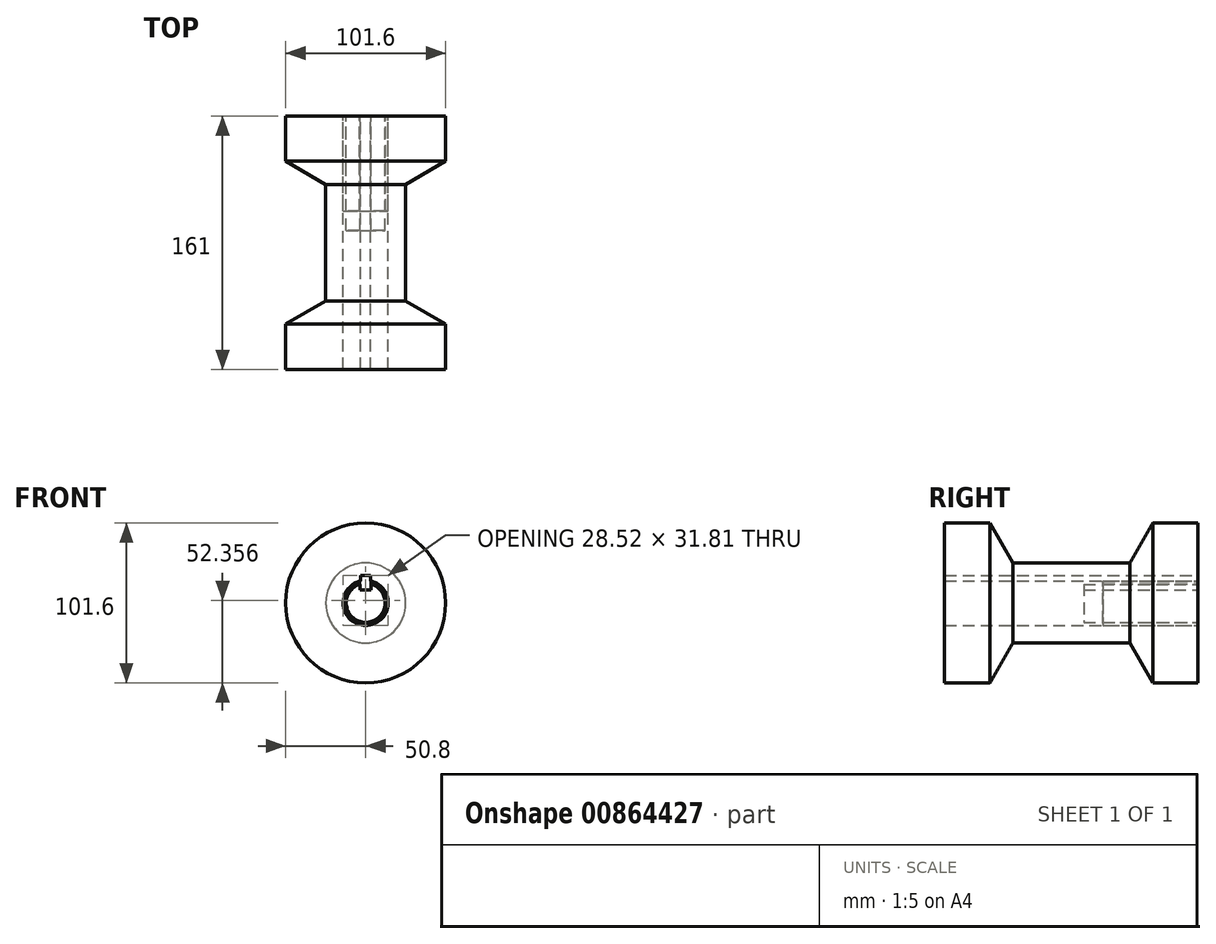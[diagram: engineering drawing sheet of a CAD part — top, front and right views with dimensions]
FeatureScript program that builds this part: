
annotation { "Feature Type Name" : "Feature", "Feature Type Description" : "" }
export const myFeature = defineFeature(function(context is Context, id is Id, definition is map)
    precondition{}
    {
        {
            var Q0;
            Q0=qCreatedBy(makeId("Front.planeOp"),FACE);
            var sketch = newSketch(context, id + "F0", { "sketchPlane" : qUnion([Q0])});
            skCircle(sketch, "E0", {"center": v(0, 0) * mm, "radius": 14.29 * mm});
            skCircle(sketch, "E1", {"center": v(0, 0) * mm, "radius": 12.5 * mm});
            skSolve(sketch);
        }
        {
            var Q0;
            Q0 = qSketchRegion(id + "F0", true);
            extrude(context, id + "F1", {"entities" : qUnion([Q0]), "depth" : 60.32 * mm, "offsetDistance" : 25.4 * mm});
        }
        {
            var Q0;
            Q0=qCreatedBy(makeId("Front.planeOp"),FACE);
            var sketch = newSketch(context, id + "F2", { "sketchPlane" : qUnion([Q0])});
            skLineSegment(sketch, "E2.bottom", {"start": v(-3.82, 0) * mm, "end": v(3.18, 0) * mm, "construction": true});
            skLineSegment(sketch, "E2.top", {"start": v(-3.83, 6.82) * mm, "end": v(3.18, 6.82) * mm});
            skLineSegment(sketch, "E2.left", {"start": v(-3.82, 0) * mm, "end": v(-3.83, 6.82) * mm, "construction": true});
            skLineSegment(sketch, "E2.right", {"start": v(3.18, 0) * mm, "end": v(3.18, 6.82) * mm, "construction": true});
            skPoint(sketch, "E3", {"position": v(0, -14.29) * mm});
            skLineSegment(sketch, "E4.0", {"start": v(-3.83, 13.65) * mm, "end": v(3.18, 13.65) * mm});
            skLineSegment(sketch, "E5", {"start": v(-3.83, 13.65) * mm, "end": v(-3.83, 6.82) * mm});
            skLineSegment(sketch, "E6", {"start": v(3.18, 13.65) * mm, "end": v(3.18, 6.82) * mm});
            skSolve(sketch);
        }
        {
            var Q0;
            Q0 = qSketchRegion(id + "F2", true);
            extrude(context, id + "F3", {"entities" : qUnion([Q0]), "operationType" : NewBodyOperationType.REMOVE, "endBound" : BoundingType.THROUGH_ALL, "depth" : 59.53 * mm, "offsetDistance" : 25.4 * mm});
        }
        {
            var Q0;
            Q0=qCreatedBy(makeId("Front.planeOp"),FACE);
            var sketch = newSketch(context, id + "F4", { "sketchPlane" : qUnion([Q0])});
            skLineSegment(sketch, "E7.bottom", {"start": v(-3.18, 17.46) * mm, "end": v(3.17, 17.46) * mm});
            skLineSegment(sketch, "E7.top", {"start": v(-3.5, 8.45) * mm, "end": v(3.5, 8.45) * mm});
            skLineSegment(sketch, "E7.left", {"start": v(-3.5, 13.85) * mm, "end": v(-3.5, 8.45) * mm});
            skLineSegment(sketch, "E7.right", {"start": v(3.5, 13.85) * mm, "end": v(3.5, 8.45) * mm});
            skLineSegment(sketch, "E8", {"start": v(0, 42.45) * mm, "end": v(0, 0) * mm, "construction": true});
            skPoint(sketch, "E9", {"position": v(0, -14.29) * mm});
            skPoint(sketch, "E10", {"position": v(0, -12.5) * mm});
            skLineSegment(sketch, "E11", {"start": v(-3.5, 13.85) * mm, "end": v(-3.18, 13.85) * mm});
            skCircle(sketch, "E12.0", {"center": v(0, 0) * mm, "radius": 14.29 * mm, "construction": true});
            skLineSegment(sketch, "E13", {"start": v(-3.18, 13.85) * mm, "end": v(-3.18, 17.46) * mm});
            skLineSegment(sketch, "E14.MirrorCS", {"start": v(3.17, 13.85) * mm, "end": v(3.17, 17.46) * mm});
            skLineSegment(sketch, "E15.MirrorCS", {"start": v(3.5, 13.85) * mm, "end": v(3.18, 13.85) * mm});
            skPoint(sketch, "E16.orphan", {"position": v(3.5, 17.46) * mm});
            skPoint(sketch, "E17.orphan", {"position": v(-3.5, 17.46) * mm});
            skSolve(sketch);
        }
        {
            var Q0;
            Q0=qCreatedBy(makeId("Front.planeOp"),FACE);
            var sketch = newSketch(context, id + "F5", { "sketchPlane" : qUnion([Q0])});
            skArc(sketch, "E18", {"start": v(-3.56, 11.8) * mm, "mid": v(0, -12.33) * mm, "end": v(3.56, 11.8) * mm});
            skLineSegment(sketch, "E19", {"start": v(-3.56, 11.8) * mm, "end": v(-3.56, 8.32) * mm});
            skLineSegment(sketch, "E20", {"start": v(0, 8.32) * mm, "end": v(-3.56, 8.32) * mm});
            skLineSegment(sketch, "E21.MirrorCS", {"start": v(0, 8.32) * mm, "end": v(3.56, 8.32) * mm});
            skLineSegment(sketch, "E22.MirrorCS", {"start": v(3.56, 11.8) * mm, "end": v(3.56, 8.32) * mm});
            skSolve(sketch);
        }
        {
            var Q0;
            Q0 = qSketchRegion(id + "F5", true);
            extrude(context, id + "F6", {"entities" : qUnion([Q0]), "endBound" : BoundingType.THROUGH_ALL, "depth" : 25.4 * mm, "offsetDistance" : 25.4 * mm});
        }
        {
            var Q0;
            Q0=qCreatedBy(makeId("Front.planeOp"),FACE);
            var sketch = newSketch(context, id + "F7", { "sketchPlane" : qUnion([Q0])});
            skLineSegment(sketch, "E23", {"start": v(-3.56, 21.02) * mm, "end": v(-3.56, 8.32) * mm});
            skLineSegment(sketch, "E24.MirrorCS", {"start": v(3.56, 21.02) * mm, "end": v(3.56, 8.32) * mm});
            skLineSegment(sketch, "E25", {"start": v(-3.56, 21.02) * mm, "end": v(3.56, 21.02) * mm});
            skLineSegment(sketch, "E26", {"start": v(-3.56, 8.32) * mm, "end": v(3.56, 8.32) * mm});
            skSolve(sketch);
        }
        {
            var Q0;
            Q0=makeQuery(id+"F7.imprint","IMPRINT",FACE,{"disambiguationData":[TD([[makeQuery(id+"F7.imprint","IMPRINT",EDGE,{"derivedFrom":sQuery(id+"F7.wireOp",EDGE,"E23")}),1.0]])]});
            extrude(context, id + "F8", {"entities" : qUnion([Q0]), "operationType" : NewBodyOperationType.REMOVE, "endBound" : BoundingType.THROUGH_ALL, "depth" : 25.4 * mm, "offsetDistance" : 25.4 * mm});
        }
        {
            var Q0;
            Q0=qCreatedBy(makeId("Front.planeOp"),FACE);
            var sketch = newSketch(context, id + "F9", { "sketchPlane" : qUnion([Q0])});
            skArc(sketch, "E27", {"start": v(-3.18, 14) * mm, "mid": v(0, -14.35) * mm, "end": v(3.18, 14) * mm});
            skCircle(sketch, "E28", {"center": v(0, 0) * mm, "radius": 50.8 * mm});
            skLineSegment(sketch, "E29", {"start": v(3.17, 17.46) * mm, "end": v(3.18, 14) * mm});
            skLineSegment(sketch, "E30.MirrorCS", {"start": v(-3.17, 17.46) * mm, "end": v(-3.18, 14) * mm});
            skLineSegment(sketch, "E31", {"start": v(3.17, 17.46) * mm, "end": v(-3.17, 17.46) * mm});
            skPoint(sketch, "E32.orphan", {"position": v(-3.17, 24.6) * mm});
            skPoint(sketch, "E33.orphan", {"position": v(3.17, 24.6) * mm});
            skPoint(sketch, "E34.orphan", {"position": v(-3.18, 4.09) * mm});
            skPoint(sketch, "E35.orphan", {"position": v(3.18, 4.09) * mm});
            skSolve(sketch);
        }
        {
            var Q0;
            Q0 = qSketchRegion(id + "F9", true);
            extrude(context, id + "F10", {"entities" : qUnion([Q0]), "endBound" : BoundingType.THROUGH_ALL, "depth" : 25.4 * mm, "offsetDistance" : 25.4 * mm});
        }
        {
            var Q0;
            Q0=qCreatedBy(makeId("Right.planeOp"),FACE);
            var sketch = newSketch(context, id + "F11", { "sketchPlane" : qUnion([Q0])});
            skLineSegment(sketch, "E36", {"start": v(-133.7, 53.34) * mm, "end": v(-117.57, 25.4) * mm});
            skLineSegment(sketch, "E37", {"start": v(-117.57, 25.4) * mm, "end": v(-43.44, 25.4) * mm});
            skLineSegment(sketch, "E38", {"start": v(-43.44, 25.4) * mm, "end": v(-27.3, 53.34) * mm});
            skLineSegment(sketch, "E39", {"start": v(-133.7, 53.34) * mm, "end": v(-27.3, 53.34) * mm});
            skLineSegment(sketch, "E40", {"start": v(0, 0) * mm, "end": v(95.02, 0) * mm, "construction": true});
            skSolve(sketch);
        }
        {
            var Q0;
            Q0 = qSketchRegion(id + "F11", true);
            var Q1;
            Q1=sQuery(id+"F11.wireOp",EDGE,"E40");
            revolve(context, id + "F12", {"operationType" : NewBodyOperationType.REMOVE, "surfaceOperationType" : NewSurfaceOperationType.NEW, "entities" : qUnion([Q0]), "axis" : qUnion([Q1]), "revolveType" : RevolveType.FULL, "oppositeDirection" : true});
        }
    });
